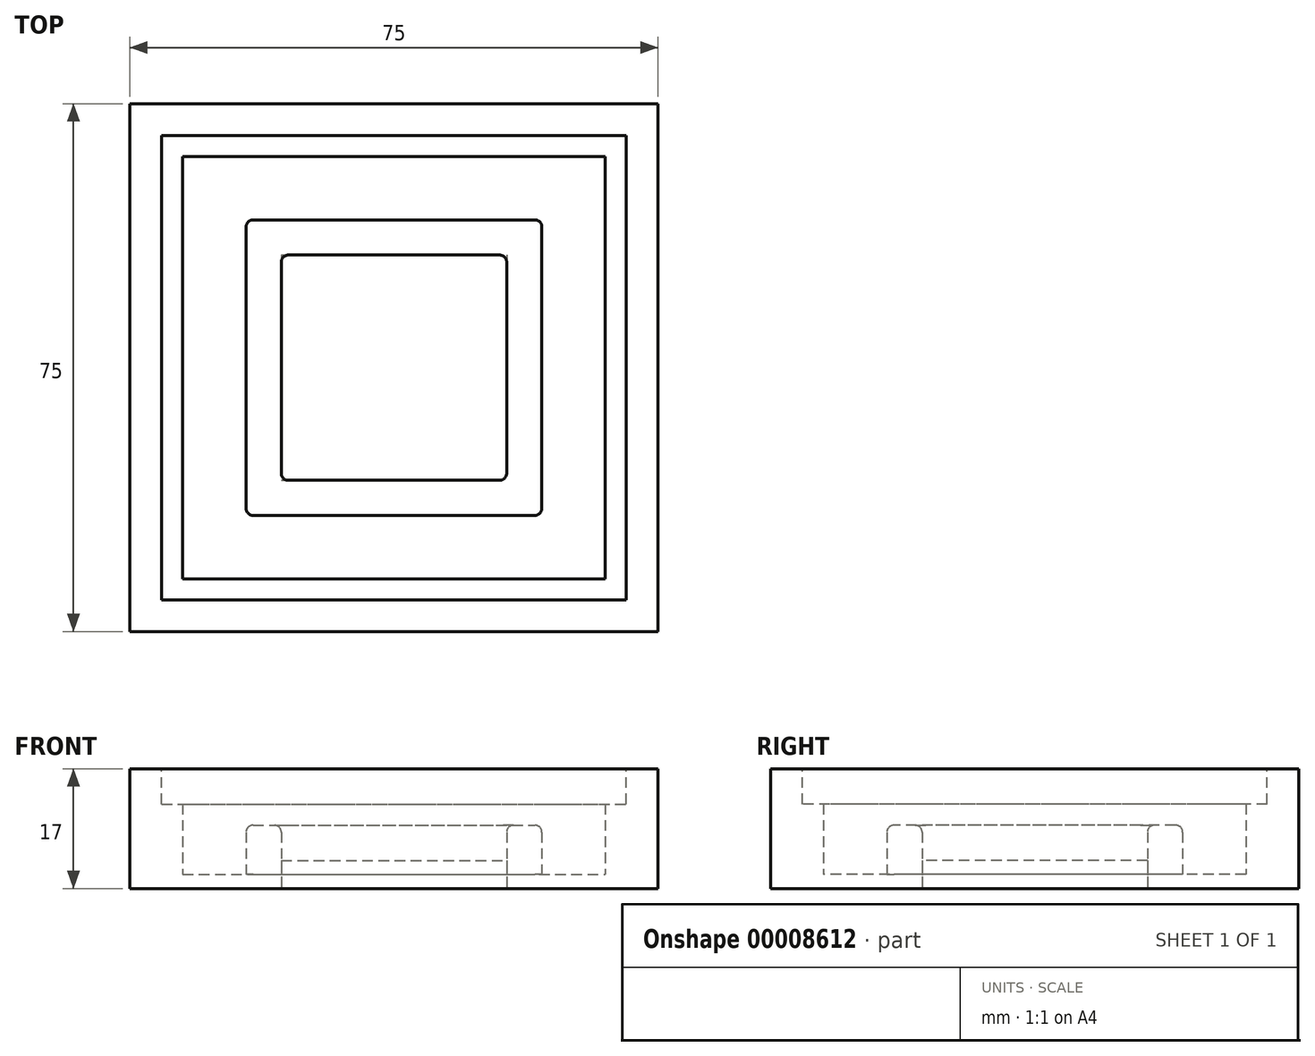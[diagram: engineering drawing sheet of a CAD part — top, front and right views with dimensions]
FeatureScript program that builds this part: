
annotation { "Feature Type Name" : "Feature", "Feature Type Description" : "" }
export const myFeature = defineFeature(function(context is Context, id is Id, definition is map)
    precondition{}
    {
        {
            var Q0;
            Q0=qCreatedBy(makeId("Top.planeOp"),FACE);
            var sketch = newSketch(context, id + "F0", { "sketchPlane" : qUnion([Q0])});
            skLineSegment(sketch, "E0.bottom", {"start": v(0, 0) * mm, "end": v(32, 0) * mm});
            skLineSegment(sketch, "E0.top", {"start": v(0, -32) * mm, "end": v(32, -32) * mm});
            skLineSegment(sketch, "E0.left", {"start": v(0, 0) * mm, "end": v(0, -32) * mm});
            skLineSegment(sketch, "E0.right", {"start": v(32, 0) * mm, "end": v(32, -32) * mm});
            skLineSegment(sketch, "E1.0", {"start": v(-5, 5) * mm, "end": v(37, 5) * mm});
            skLineSegment(sketch, "E1.1", {"start": v(-5, 5) * mm, "end": v(-5, -37) * mm});
            skLineSegment(sketch, "E1.2", {"start": v(-5, -37) * mm, "end": v(37, -37) * mm});
            skLineSegment(sketch, "E1.3", {"start": v(37, 5) * mm, "end": v(37, -37) * mm});
            skLineSegment(sketch, "E2.0", {"start": v(-14, 14) * mm, "end": v(-14, -46) * mm});
            skLineSegment(sketch, "E2.1", {"start": v(-14, 14) * mm, "end": v(46, 14) * mm});
            skLineSegment(sketch, "E2.2", {"start": v(46, 14) * mm, "end": v(46, -46) * mm});
            skLineSegment(sketch, "E2.3", {"start": v(-14, -46) * mm, "end": v(46, -46) * mm});
            skLineSegment(sketch, "E3.0", {"start": v(-21.5, 21.5) * mm, "end": v(53.5, 21.5) * mm});
            skLineSegment(sketch, "E3.1", {"start": v(-21.5, 21.5) * mm, "end": v(-21.5, -53.5) * mm});
            skLineSegment(sketch, "E3.2", {"start": v(-21.5, -53.5) * mm, "end": v(53.5, -53.5) * mm});
            skLineSegment(sketch, "E3.3", {"start": v(53.5, 21.5) * mm, "end": v(53.5, -53.5) * mm});
            skSolve(sketch);
        }
        {
            var Q0;
            Q0=makeQuery(id+"F0.imprint","IMPRINT",FACE,{"disambiguationData":[TD([[makeQuery(id+"F0.imprint","IMPRINT",EDGE,{"derivedFrom":sQuery(id+"F0.wireOp",EDGE,"E0.bottom")}),1.0]])]});
            extrude(context, id + "F1", {"entities" : qUnion([Q0]), "depth" : 9 * mm});
        }
        {
            var Q0;
            Q0=makeQuery(id+"F0.imprint","IMPRINT",FACE,{"disambiguationData":[TD([[makeQuery(id+"F0.imprint","IMPRINT",EDGE,{"derivedFrom":sQuery(id+"F0.wireOp",EDGE,"E0.bottom")}),-1.0]])]});
            extrude(context, id + "F2", {"entities" : qUnion([Q0]), "depth" : 4 * mm});
        }
        {
            var Q0;
            Q0=makeQuery(id+"F0.imprint","IMPRINT",FACE,{"disambiguationData":[TD([[makeQuery(id+"F0.imprint","IMPRINT",EDGE,{"derivedFrom":sQuery(id+"F0.wireOp",EDGE,"E2.0")}),-1.0]])]});
            extrude(context, id + "F3", {"entities" : qUnion([Q0]), "depth" : 17 * mm});
        }
        {
            var Q0;
            Q0=makeQuery(id+"F0.imprint","IMPRINT",FACE,{"disambiguationData":[TD([[makeQuery(id+"F0.imprint","IMPRINT",EDGE,{"derivedFrom":sQuery(id+"F0.wireOp",EDGE,"E1.0")}),1.0]])]});
            extrude(context, id + "F4", {"entities" : qUnion([Q0]), "operationType" : NewBodyOperationType.ADD, "depth" : 2 * mm});
        }
        {
            var Q0;
            Q0=makeQuery(id+"F1.opExtrude","SWEPT_EDGE",EDGE,{"disambiguationData":[OSD([sQuery(id+"F0.wireOp",EDGE,"E1.0"),sQuery(id+"F0.wireOp",EDGE,"E1.3")])]});
            var Q1;
            Q1=makeQuery(id+"F1.opExtrude","SWEPT_EDGE",EDGE,{"disambiguationData":[OSD([sQuery(id+"F0.wireOp",EDGE,"E1.1"),sQuery(id+"F0.wireOp",EDGE,"E1.2")])]});
            var Q2;
            Q2=makeQuery(id+"F1.opExtrude","SWEPT_EDGE",EDGE,{"disambiguationData":[OSD([sQuery(id+"F0.wireOp",EDGE,"E1.2"),sQuery(id+"F0.wireOp",EDGE,"E1.3")])]});
            var Q3;
            Q3=makeQuery(id+"F1.opExtrude","SWEPT_EDGE",EDGE,{"disambiguationData":[OSD([sQuery(id+"F0.wireOp",EDGE,"E1.0"),sQuery(id+"F0.wireOp",EDGE,"E1.1")])]});
            var Q4;
            Q4=makeQuery(id+"F1.opExtrude","SWEPT_EDGE",EDGE,{"disambiguationData":[OSD([sQuery(id+"F0.wireOp",EDGE,"E0.bottom"),sQuery(id+"F0.wireOp",EDGE,"E0.right")])]});
            var Q5;
            Q5=makeQuery(id+"F1.opExtrude","SWEPT_EDGE",EDGE,{"disambiguationData":[OSD([sQuery(id+"F0.wireOp",EDGE,"E0.top"),sQuery(id+"F0.wireOp",EDGE,"E0.right")])]});
            var Q6;
            Q6=makeQuery(id+"F1.opExtrude","SWEPT_EDGE",EDGE,{"disambiguationData":[OSD([sQuery(id+"F0.wireOp",EDGE,"E0.bottom"),sQuery(id+"F0.wireOp",EDGE,"E0.left")])]});
            var Q7;
            Q7=makeQuery(id+"F1.opExtrude","SWEPT_EDGE",EDGE,{"disambiguationData":[OSD([sQuery(id+"F0.wireOp",EDGE,"E0.top"),sQuery(id+"F0.wireOp",EDGE,"E0.left")])]});
            fillet(context, id + "F5", {"entities" : qUnion([Q0, Q1, Q2, Q3, Q4, Q5, Q6, Q7]), "radius" : 1 * mm, "tangentPropagation" : true, "allowEdgeOverflow" : false});
        }
        {
            var Q0;
            Q0=makeQuery(id+"F1.opExtrude","CAP_EDGE",EDGE,{"disambiguationData":[OSD([sQuery(id+"F0.wireOp",EDGE,"E1.3")])],"isStart":false});
            var Q1;
            Q1=makeQuery(id+"F1.opExtrude","CAP_EDGE",EDGE,{"disambiguationData":[OSD([sQuery(id+"F0.wireOp",EDGE,"E1.0")])],"isStart":false});
            fillet(context, id + "F6", {"entities" : qUnion([Q0, Q1]), "radius" : 1 * mm, "tangentPropagation" : true, "allowEdgeOverflow" : false});
        }
        {
            var Q0;
            Q0=makeQuery(id+"F1.opExtrude","CAP_EDGE",EDGE,{"disambiguationData":[OSD([sQuery(id+"F0.wireOp",EDGE,"E0.right")])],"isStart":false});
            var Q1;
            Q1=makeQuery(id+"F1.opExtrude","CAP_EDGE",EDGE,{"disambiguationData":[OSD([sQuery(id+"F0.wireOp",EDGE,"E0.top")])],"isStart":false});
            var Q2;
            Q2=makeQuery(id+"F1.opExtrude","CAP_EDGE",EDGE,{"disambiguationData":[OSD([sQuery(id+"F0.wireOp",EDGE,"E0.left")])],"isStart":false});
            var Q3;
            Q3=makeQuery(id+"F1.opExtrude","CAP_EDGE",EDGE,{"disambiguationData":[OSD([sQuery(id+"F0.wireOp",EDGE,"E0.bottom")])],"isStart":false});
            fillet(context, id + "F7", {"entities" : qUnion([Q0, Q1, Q2, Q3]), "radius" : 1 * mm, "tangentPropagation" : true, "allowEdgeOverflow" : false});
        }
        {
            var Q0;
            Q0=makeQuery(id+"F3.opExtrude","CAP_FACE",FACE,{"disambiguationData":[OSD([sQuery(id+"F0.wireOp",EDGE,"E2.0"),sQuery(id+"F0.wireOp",EDGE,"E2.1"),sQuery(id+"F0.wireOp",EDGE,"E2.2"),sQuery(id+"F0.wireOp",EDGE,"E2.3"),sQuery(id+"F0.wireOp",EDGE,"E3.0"),sQuery(id+"F0.wireOp",EDGE,"E3.1"),sQuery(id+"F0.wireOp",EDGE,"E3.2"),sQuery(id+"F0.wireOp",EDGE,"E3.3")])],"isStart":false});
            var sketch = newSketch(context, id + "F8", { "sketchPlane" : qUnion([Q0])});
            skLineSegment(sketch, "E4.0", {"start": v(-14, 14) * mm, "end": v(46, 14) * mm});
            skLineSegment(sketch, "E5.0", {"start": v(-14, 14) * mm, "end": v(-14, -46) * mm});
            skLineSegment(sketch, "E6.0", {"start": v(-14, -46) * mm, "end": v(46, -46) * mm});
            skLineSegment(sketch, "E7.0", {"start": v(46, 14) * mm, "end": v(46, -46) * mm});
            skLineSegment(sketch, "E8.0", {"start": v(-17, 17) * mm, "end": v(49, 17) * mm});
            skLineSegment(sketch, "E8.1", {"start": v(-17, 17) * mm, "end": v(-17, -49) * mm});
            skLineSegment(sketch, "E8.2", {"start": v(-17, -49) * mm, "end": v(49, -49) * mm});
            skLineSegment(sketch, "E8.3", {"start": v(49, 17) * mm, "end": v(49, -49) * mm});
            skSolve(sketch);
        }
        {
            var Q0;
            Q0=makeQuery(id+"F8.imprint","IMPRINT",FACE,{"disambiguationData":[TD([[makeQuery(id+"F8.imprint","IMPRINT",EDGE,{"derivedFrom":sQuery(id+"F8.wireOp",EDGE,"E4.0")}),1.0]])]});
            extrude(context, id + "F9", {"entities" : qUnion([Q0]), "operationType" : NewBodyOperationType.REMOVE, "oppositeDirection" : true, "depth" : 5 * mm});
        }
    });
